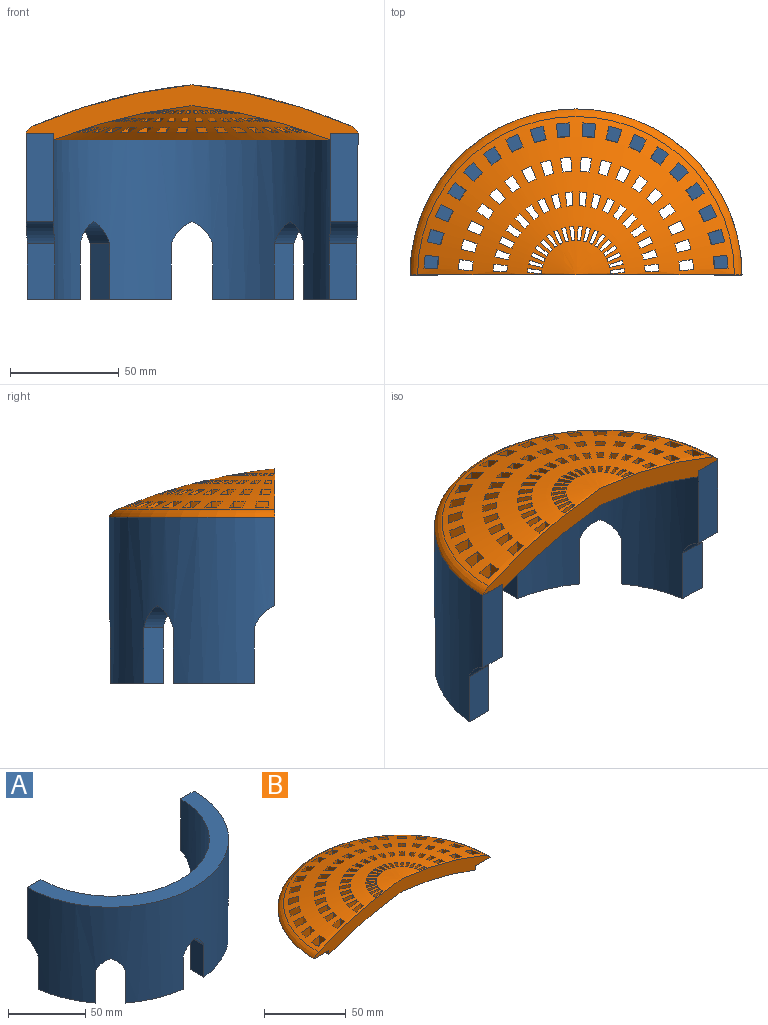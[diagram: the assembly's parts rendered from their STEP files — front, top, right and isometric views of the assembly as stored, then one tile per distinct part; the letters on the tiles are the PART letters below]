
ASSEMBLY  parts=2 mates=1
PART A: 25 faces, bbox 152.4x76.2x76.2 mm
  f0: cylinder r=63.75mm len=127.51mm, axis (0,0,-1), area 12814.7mm2, adj f2,f3,f4,f5,f6,f7,f8,f9
  f1: cylinder r=76.2mm len=152.4mm, axis (0,0,-1), area 15796.6mm2, adj f2,f3,f4,f5,f6,f7,f8,f9
  f2: plane 152.4x76.2mm, normal (0,0,1), area 2736.1mm2, adj f0,f1,f23,f24
  f3: plane 25.4x12.56mm, normal (0,1,0), area 319.1mm2, adj f0,f1,f4,f5
  f4: cylinder r=16.44mm len=13.16mm, axis (-1,0,0), area 179.7mm2, adj f0,f1,f3,f24
  f5: plane 37.2x24.29mm, normal (0,0,-1), area 446.2mm2, adj f0,f1,f3,f6
  f6: plane 25.4x8.88mm, normal (-0.71,-0.71,0), area 319.1mm2, adj f0,f1,f5,f9
  f7: plane 25.4x8.88mm, normal (0.71,0.71,0), area 319.1mm2, adj f0,f1,f8,f10
  f8: cylinder r=16.44mm len=16.04mm, axis (-0.71,0.71,0), area 179.7mm2, adj f0,f1,f7,f9
  f9: cylinder r=16.44mm len=16.04mm, axis (-0.71,0.71,0), area 179.7mm2, adj f0,f1,f6,f8
  f10: plane 37.2x24.29mm, normal (0,0,-1), area 446.2mm2, adj f0,f1,f7,f11
  f11: plane 25.4x12.56mm, normal (-1,0,0), area 319.1mm2, adj f0,f1,f10,f14
  f12: plane 25.4x12.56mm, normal (1,0,0), area 319.1mm2, adj f0,f1,f13,f15
  f13: cylinder r=16.44mm len=13.16mm, axis (0,1,0), area 179.7mm2, adj f0,f1,f12,f14
  f14: cylinder r=16.44mm len=13.16mm, axis (0,1,0), area 179.7mm2, adj f0,f1,f11,f13
  f15: plane 37.2x24.29mm, normal (0,0,-1), area 446.2mm2, adj f0,f1,f12,f16
  f16: plane 25.4x8.88mm, normal (-0.71,0.71,0), area 319.1mm2, adj f0,f1,f15,f19
  f17: plane 25.4x8.88mm, normal (0.71,-0.71,0), area 319.1mm2, adj f0,f1,f18,f20
  f18: cylinder r=16.44mm len=16.04mm, axis (0.71,0.71,0), area 179.7mm2, adj f0,f1,f17,f19
  f19: cylinder r=16.44mm len=16.04mm, axis (0.71,0.71,0), area 179.7mm2, adj f0,f1,f16,f18
  f20: plane 37.2x24.29mm, normal (0,0,-1), area 446.2mm2, adj f0,f1,f17,f21
  f21: plane 25.4x12.56mm, normal (0,1,0), area 319.1mm2, adj f0,f1,f20,f22
  f22: cylinder r=16.44mm len=13.16mm, axis (1,0,0), area 179.7mm2, adj f0,f1,f21,f23
  f23: plane 40.64x12.45mm, normal (0,1,0), area 505.7mm2, adj f0,f1,f2,f22
  f24: plane 40.64x12.45mm, normal (0,1,0), area 505.7mm2, adj f0,f1,f2,f4
PART B: 276 faces, bbox 166.3x83.1x25.3 mm
  f0: revolved ~145.41x72.71mm, area 6921.5mm2, adj f3,f4,f5,f6,f7,f8,f9,f10
  f1: plane 152.4x76.2mm, normal (0,0,-1), area 2121.8mm2, adj f3,f4,f5,f222,f223,f224,f225,f226
  f2: revolved ~127x63.5mm, area 5531.8mm2, adj f4,f5,f6,f7,f8,f9,f10,f11
  f3: torus R=70.05mm, axis (0,0,1), area 1172.7mm2, adj f0,f1,f5
  f4: cylinder r=63.5mm len=127mm, axis (0,0,1), area 1327.7mm2, adj f0,f1,f2,f5,f223,f224,f226,f227
  f5: plane 152.4x25.31mm, normal (0,-1,0), area 1361.2mm2, adj f0,f1,f2,f3,f4
  f6: cylinder r=31.75mm len=9.8mm, axis (0,0,1), area 27.1mm2, adj f0,f2,f7,f9
  f7: plane 11.45x6.3mm, normal (-0.99,0.13,0), area 62.4mm2, adj f0,f2,f6,f8
  f8: cylinder r=38.1mm len=9.86mm, axis (0,0,1), area 32.8mm2, adj f0,f2,f7,f9
  f9: plane 11.45x6.34mm, normal (1,-0.04,0), area 62.4mm2, adj f0,f2,f6,f8
  f10: plane 12.11x6.2mm, normal (0.22,0.98,0), area 63.7mm2, adj f0,f2,f11,f13
  f11: cylinder r=47.62mm len=9.98mm, axis (0,0,1), area 41.5mm2, adj f0,f2,f10,f12
  f12: plane 12.11x6.06mm, normal (-0.3,-0.95,0), area 63.7mm2, adj f0,f2,f11,f13
  f13: cylinder r=53.98mm len=10.07mm, axis (0,0,1), area 47.4mm2, adj f0,f2,f10,f12
  f14: plane 11.45x5.87mm, normal (0.38,0.92,0), area 62.4mm2, adj f0,f2,f15,f17
  f15: cylinder r=31.75mm len=9.8mm, axis (0,0,1), area 27.1mm2, adj f0,f2,f14,f16
  f16: plane 11.45x5.63mm, normal (-0.46,-0.89,0), area 62.4mm2, adj f0,f2,f15,f17
  f17: cylinder r=38.1mm len=9.86mm, axis (0,0,1), area 32.8mm2, adj f0,f2,f14,f16
  f18: cylinder r=38.1mm len=9.86mm, axis (0,0,1), area 32.8mm2, adj f0,f2,f19,f21
  f19: plane 11.45x6.2mm, normal (0.22,0.98,0), area 62.4mm2, adj f0,f2,f18,f20
  f20: cylinder r=31.75mm len=9.8mm, axis (0,0,1), area 27.1mm2, adj f0,f2,f19,f21
  f21: plane 11.45x6.06mm, normal (-0.3,-0.95,0), area 62.4mm2, adj f0,f2,f18,f20
  f22: plane 12.11x6.34mm, normal (-0.04,1,0), area 63.7mm2, adj f0,f2,f23,f25
  f23: cylinder r=53.98mm len=10.07mm, axis (0,0,1), area 47.4mm2, adj f0,f2,f22,f24
  f24: plane 12.11x6.3mm, normal (0.13,-0.99,0), area 63.7mm2, adj f0,f2,f23,f25
  f25: cylinder r=47.62mm len=9.98mm, axis (0,0,1), area 41.5mm2, adj f0,f2,f22,f24
  f26: plane 10.86x6.2mm, normal (0.22,0.98,0), area 61.5mm2, adj f0,f2,f27,f29
  f27: cylinder r=15.88mm len=9.66mm, axis (0,0,1), area 13.4mm2, adj f0,f2,f26,f28
  f28: plane 10.86x6.06mm, normal (-0.3,-0.95,0), area 61.5mm2, adj f0,f2,f27,f29
  f29: cylinder r=22.23mm len=9.71mm, axis (0,0,1), area 18.8mm2, adj f0,f2,f26,f28
  f30: cylinder r=22.23mm len=9.71mm, axis (0,0,1), area 18.8mm2, adj f0,f2,f31,f33
  f31: plane 10.86x5.36mm, normal (0.54,0.84,0), area 61.5mm2, adj f0,f2,f30,f32
  f32: cylinder r=15.88mm len=9.66mm, axis (0,0,1), area 13.4mm2, adj f0,f2,f31,f33
  f33: plane 10.86x5.04mm, normal (-0.61,-0.79,0), area 61.5mm2, adj f0,f2,f30,f32
  f34: plane 10.86x5.87mm, normal (0.38,0.92,0), area 61.5mm2, adj f0,f2,f35,f37
  f35: cylinder r=15.88mm len=9.66mm, axis (0,0,1), area 13.4mm2, adj f0,f2,f34,f36
  f36: plane 10.86x5.63mm, normal (-0.46,-0.89,0), area 61.5mm2, adj f0,f2,f35,f37
  f37: cylinder r=22.23mm len=9.71mm, axis (0,0,1), area 18.8mm2, adj f0,f2,f34,f36
  f38: plane 11.45x4.68mm, normal (-0.68,0.74,0), area 62.4mm2, adj f0,f2,f39,f41
  f39: cylinder r=38.1mm len=9.86mm, axis (0,0,1), area 32.8mm2, adj f0,f2,f38,f40
  f40: plane 11.45x4.68mm, normal (0.74,-0.68,0), area 62.4mm2, adj f0,f2,f39,f41
  f41: cylinder r=31.75mm len=9.8mm, axis (0,0,1), area 27.1mm2, adj f0,f2,f38,f40
  f42: plane 10.86x6.06mm, normal (-0.95,0.3,0), area 61.5mm2, adj f0,f2,f43,f45
  f43: cylinder r=22.23mm len=9.71mm, axis (0,0,1), area 18.8mm2, adj f0,f2,f42,f44
  f44: plane 10.86x6.2mm, normal (0.98,-0.22,0), area 61.5mm2, adj f0,f2,f43,f45
  f45: cylinder r=15.88mm len=9.66mm, axis (0,0,1), area 13.4mm2, adj f0,f2,f42,f44
  f46: plane 10.86x5.04mm, normal (-0.79,0.61,0), area 61.5mm2, adj f0,f2,f47,f49
  f47: cylinder r=22.23mm len=9.71mm, axis (0,0,1), area 18.8mm2, adj f0,f2,f46,f48
  f48: plane 10.86x5.36mm, normal (0.84,-0.54,0), area 61.5mm2, adj f0,f2,f47,f49
  f49: cylinder r=15.88mm len=9.66mm, axis (0,0,1), area 13.4mm2, adj f0,f2,f46,f48
  f50: plane 10.86x5.63mm, normal (-0.89,0.46,0), area 61.5mm2, adj f0,f2,f51,f53
  f51: cylinder r=22.23mm len=9.71mm, axis (0,0,1), area 18.8mm2, adj f0,f2,f50,f52
  f52: plane 10.86x5.87mm, normal (0.92,-0.38,0), area 61.5mm2, adj f0,f2,f51,f53
  f53: cylinder r=15.88mm len=9.66mm, axis (0,0,1), area 13.4mm2, adj f0,f2,f50,f52
  f54: plane 12.11x5.87mm, normal (-0.38,0.92,0), area 63.7mm2, adj f0,f2,f55,f57
  f55: cylinder r=53.98mm len=10.07mm, axis (0,0,1), area 47.4mm2, adj f0,f2,f54,f56
  f56: plane 12.11x5.63mm, normal (0.46,-0.89,0), area 63.7mm2, adj f0,f2,f55,f57
  f57: cylinder r=47.62mm len=9.98mm, axis (0,0,1), area 41.5mm2, adj f0,f2,f54,f56
  f58: plane 11.45x6.06mm, normal (-0.95,0.3,0), area 62.4mm2, adj f0,f2,f59,f61
  f59: cylinder r=38.1mm len=9.86mm, axis (0,0,1), area 32.8mm2, adj f0,f2,f58,f60
  f60: plane 11.45x6.2mm, normal (0.98,-0.22,0), area 62.4mm2, adj f0,f2,f59,f61
  f61: cylinder r=31.75mm len=9.8mm, axis (0,0,1), area 27.1mm2, adj f0,f2,f58,f60
  f62: plane 11.45x5.04mm, normal (-0.79,0.61,0), area 62.4mm2, adj f0,f2,f63,f65
  f63: cylinder r=38.1mm len=9.86mm, axis (0,0,1), area 32.8mm2, adj f0,f2,f62,f64
  f64: plane 11.45x5.36mm, normal (0.84,-0.54,0), area 62.4mm2, adj f0,f2,f63,f65
  f65: cylinder r=31.75mm len=9.8mm, axis (0,0,1), area 27.1mm2, adj f0,f2,f62,f64
  f66: plane 11.45x5.63mm, normal (-0.89,0.46,0), area 62.4mm2, adj f0,f2,f67,f69
  f67: cylinder r=38.1mm len=9.86mm, axis (0,0,1), area 32.8mm2, adj f0,f2,f66,f68
  f68: plane 11.45x5.87mm, normal (0.92,-0.38,0), area 62.4mm2, adj f0,f2,f67,f69
  f69: cylinder r=31.75mm len=9.8mm, axis (0,0,1), area 27.1mm2, adj f0,f2,f66,f68
  f70: plane 10.86x5.36mm, normal (-0.54,0.84,0), area 61.5mm2, adj f0,f2,f71,f73
  f71: cylinder r=22.23mm len=9.71mm, axis (0,0,1), area 18.8mm2, adj f0,f2,f70,f72
  f72: plane 10.86x5.04mm, normal (0.61,-0.79,0), area 61.5mm2, adj f0,f2,f71,f73
  f73: cylinder r=15.88mm len=9.66mm, axis (0,0,1), area 13.4mm2, adj f0,f2,f70,f72
  f74: cylinder r=31.75mm len=9.8mm, axis (0,0,1), area 27.1mm2, adj f0,f2,f75,f77
  f75: plane 11.45x4.68mm, normal (-0.74,-0.68,0), area 62.4mm2, adj f0,f2,f74,f76
  f76: cylinder r=38.1mm len=9.86mm, axis (0,0,1), area 32.8mm2, adj f0,f2,f75,f77
  f77: plane 11.45x4.68mm, normal (0.68,0.74,0), area 62.4mm2, adj f0,f2,f74,f76
  f78: cylinder r=31.75mm len=9.8mm, axis (0,0,1), area 27.1mm2, adj f0,f2,f79,f81
  f79: plane 11.45x5.36mm, normal (-0.84,-0.54,0), area 62.4mm2, adj f0,f2,f78,f80
  f80: cylinder r=38.1mm len=9.86mm, axis (0,0,1), area 32.8mm2, adj f0,f2,f79,f81
  f81: plane 11.45x5.04mm, normal (0.79,0.61,0), area 62.4mm2, adj f0,f2,f78,f80
  f82: cylinder r=15.88mm len=9.66mm, axis (0,0,1), area 13.4mm2, adj f0,f2,f83,f85
  f83: plane 10.86x6.2mm, normal (-0.98,-0.22,0), area 61.5mm2, adj f0,f2,f82,f84
  f84: cylinder r=22.23mm len=9.71mm, axis (0,0,1), area 18.8mm2, adj f0,f2,f83,f85
  f85: plane 10.86x6.06mm, normal (0.95,0.3,0), area 61.5mm2, adj f0,f2,f82,f84
  f86: plane 10.86x4.68mm, normal (-0.68,0.74,0), area 61.5mm2, adj f0,f2,f87,f89
  f87: cylinder r=22.23mm len=9.71mm, axis (0,0,1), area 18.8mm2, adj f0,f2,f86,f88
  f88: plane 10.86x4.68mm, normal (0.74,-0.68,0), area 61.5mm2, adj f0,f2,f87,f89
  f89: cylinder r=15.88mm len=9.66mm, axis (0,0,1), area 13.4mm2, adj f0,f2,f86,f88
  f90: plane 11.45x5.36mm, normal (-0.54,0.84,0), area 62.4mm2, adj f0,f2,f91,f93
  f91: cylinder r=38.1mm len=9.86mm, axis (0,0,1), area 32.8mm2, adj f0,f2,f90,f92
  f92: plane 11.45x5.04mm, normal (0.61,-0.79,0), area 62.4mm2, adj f0,f2,f91,f93
  f93: cylinder r=31.75mm len=9.8mm, axis (0,0,1), area 27.1mm2, adj f0,f2,f90,f92
  f94: plane 11.45x5.87mm, normal (-0.38,0.92,0), area 62.4mm2, adj f0,f2,f95,f97
  f95: cylinder r=38.1mm len=9.86mm, axis (0,0,1), area 32.8mm2, adj f0,f2,f94,f96
  f96: plane 11.45x5.63mm, normal (0.46,-0.89,0), area 62.4mm2, adj f0,f2,f95,f97
  f97: cylinder r=31.75mm len=9.8mm, axis (0,0,1), area 27.1mm2, adj f0,f2,f94,f96
  f98: plane 12.11x6.2mm, normal (-0.22,0.98,0), area 63.7mm2, adj f0,f2,f99,f101
  f99: cylinder r=53.98mm len=10.07mm, axis (0,0,1), area 47.4mm2, adj f0,f2,f98,f100
  f100: plane 12.11x6.06mm, normal (0.3,-0.95,0), area 63.7mm2, adj f0,f2,f99,f101
  f101: cylinder r=47.62mm len=9.98mm, axis (0,0,1), area 41.5mm2, adj f0,f2,f98,f100
  f102: plane 10.86x6.34mm, normal (1,-0.04,0), area 61.5mm2, adj f0,f2,f103,f105
  f103: cylinder r=15.88mm len=9.66mm, axis (0,0,1), area 13.4mm2, adj f0,f2,f102,f104
  f104: plane 10.86x6.3mm, normal (-0.99,0.13,0), area 61.5mm2, adj f0,f2,f103,f105
  f105: cylinder r=22.23mm len=9.71mm, axis (0,0,1), area 18.8mm2, adj f0,f2,f102,f104
  f106: plane 12.11x6.34mm, normal (1,-0.04,0), area 63.7mm2, adj f0,f2,f107,f109
  f107: cylinder r=47.62mm len=9.98mm, axis (0,0,1), area 41.5mm2, adj f0,f2,f106,f108
  f108: plane 12.11x6.3mm, normal (-0.99,0.13,0), area 63.7mm2, adj f0,f2,f107,f109
  f109: cylinder r=53.98mm len=10.07mm, axis (0,0,1), area 47.4mm2, adj f0,f2,f106,f108
  f110: plane 12.11x5.63mm, normal (-0.89,0.46,0), area 63.7mm2, adj f0,f2,f111,f113
  f111: cylinder r=53.98mm len=10.07mm, axis (0,0,1), area 47.4mm2, adj f0,f2,f110,f112
  f112: plane 12.11x5.87mm, normal (0.92,-0.38,0), area 63.7mm2, adj f0,f2,f111,f113
  f113: cylinder r=47.62mm len=9.98mm, axis (0,0,1), area 41.5mm2, adj f0,f2,f110,f112
  f114: plane 12.11x5.04mm, normal (-0.79,0.61,0), area 63.7mm2, adj f0,f2,f115,f117
  f115: cylinder r=53.98mm len=10.07mm, axis (0,0,1), area 47.4mm2, adj f0,f2,f114,f116
  f116: plane 12.11x5.36mm, normal (0.84,-0.54,0), area 63.7mm2, adj f0,f2,f115,f117
  f117: cylinder r=47.62mm len=9.98mm, axis (0,0,1), area 41.5mm2, adj f0,f2,f114,f116
  f118: plane 12.11x5.36mm, normal (-0.54,0.84,0), area 63.7mm2, adj f0,f2,f119,f121
  f119: cylinder r=53.98mm len=10.07mm, axis (0,0,1), area 47.4mm2, adj f0,f2,f118,f120
  f120: plane 12.11x5.04mm, normal (0.61,-0.79,0), area 63.7mm2, adj f0,f2,f119,f121
  f121: cylinder r=47.62mm len=9.98mm, axis (0,0,1), area 41.5mm2, adj f0,f2,f118,f120
  f122: plane 12.11x4.68mm, normal (-0.68,0.74,0), area 63.7mm2, adj f0,f2,f123,f125
  f123: cylinder r=53.98mm len=10.07mm, axis (0,0,1), area 47.4mm2, adj f0,f2,f122,f124
  f124: plane 12.11x4.68mm, normal (0.74,-0.68,0), area 63.7mm2, adj f0,f2,f123,f125
  f125: cylinder r=47.62mm len=9.98mm, axis (0,0,1), area 41.5mm2, adj f0,f2,f122,f124
  f126: plane 12.11x6.06mm, normal (-0.95,0.3,0), area 63.7mm2, adj f0,f2,f127,f129
  f127: cylinder r=53.98mm len=10.07mm, axis (0,0,1), area 47.4mm2, adj f0,f2,f126,f128
  f128: plane 12.11x6.2mm, normal (0.98,-0.22,0), area 63.7mm2, adj f0,f2,f127,f129
  f129: cylinder r=47.62mm len=9.98mm, axis (0,0,1), area 41.5mm2, adj f0,f2,f126,f128
  f130: plane 12.11x6.34mm, normal (0.04,1,0), area 63.7mm2, adj f0,f2,f131,f133
  f131: cylinder r=47.62mm len=9.98mm, axis (0,0,1), area 41.5mm2, adj f0,f2,f130,f132
  f132: plane 12.11x6.3mm, normal (-0.13,-0.99,0), area 63.7mm2, adj f0,f2,f131,f133
  f133: cylinder r=53.98mm len=10.07mm, axis (0,0,1), area 47.4mm2, adj f0,f2,f130,f132
  f134: plane 11.45x6.34mm, normal (-0.04,1,0), area 62.4mm2, adj f0,f2,f135,f137
  f135: cylinder r=38.1mm len=9.86mm, axis (0,0,1), area 32.8mm2, adj f0,f2,f134,f136
  f136: plane 11.45x6.3mm, normal (0.13,-0.99,0), area 62.4mm2, adj f0,f2,f135,f137
  f137: cylinder r=31.75mm len=9.8mm, axis (0,0,1), area 27.1mm2, adj f0,f2,f134,f136
  f138: plane 11.45x6.2mm, normal (-0.22,0.98,0), area 62.4mm2, adj f0,f2,f139,f141
  f139: cylinder r=38.1mm len=9.86mm, axis (0,0,1), area 32.8mm2, adj f0,f2,f138,f140
  f140: plane 11.45x6.06mm, normal (0.3,-0.95,0), area 62.4mm2, adj f0,f2,f139,f141
  f141: cylinder r=31.75mm len=9.8mm, axis (0,0,1), area 27.1mm2, adj f0,f2,f138,f140
  f142: plane 10.86x6.34mm, normal (-0.04,1,0), area 61.5mm2, adj f0,f2,f143,f145
  f143: cylinder r=22.23mm len=9.71mm, axis (0,0,1), area 18.8mm2, adj f0,f2,f142,f144
  f144: plane 10.86x6.3mm, normal (0.13,-0.99,0), area 61.5mm2, adj f0,f2,f143,f145
  f145: cylinder r=15.88mm len=9.66mm, axis (0,0,1), area 13.4mm2, adj f0,f2,f142,f144
  f146: plane 10.86x6.2mm, normal (-0.22,0.98,0), area 61.5mm2, adj f0,f2,f147,f149
  f147: cylinder r=22.23mm len=9.71mm, axis (0,0,1), area 18.8mm2, adj f0,f2,f146,f148
  f148: plane 10.86x6.06mm, normal (0.3,-0.95,0), area 61.5mm2, adj f0,f2,f147,f149
  f149: cylinder r=15.88mm len=9.66mm, axis (0,0,1), area 13.4mm2, adj f0,f2,f146,f148
  f150: plane 10.86x5.87mm, normal (-0.38,0.92,0), area 61.5mm2, adj f0,f2,f151,f153
  f151: cylinder r=22.23mm len=9.71mm, axis (0,0,1), area 18.8mm2, adj f0,f2,f150,f152
  f152: plane 10.86x5.63mm, normal (0.46,-0.89,0), area 61.5mm2, adj f0,f2,f151,f153
  f153: cylinder r=15.88mm len=9.66mm, axis (0,0,1), area 13.4mm2, adj f0,f2,f150,f152
  f154: cylinder r=22.23mm len=9.71mm, axis (0,0,1), area 18.8mm2, adj f0,f2,f155,f157
  f155: plane 10.86x6.3mm, normal (0.99,0.13,0), area 61.5mm2, adj f0,f2,f154,f156
  f156: cylinder r=15.88mm len=9.66mm, axis (0,0,1), area 13.4mm2, adj f0,f2,f155,f157
  f157: plane 10.86x6.34mm, normal (-1,-0.04,0), area 61.5mm2, adj f0,f2,f154,f156
  f158: cylinder r=38.1mm len=9.86mm, axis (0,0,1), area 32.8mm2, adj f0,f2,f159,f161
  f159: plane 11.45x6.3mm, normal (0.99,0.13,0), area 62.4mm2, adj f0,f2,f158,f160
  f160: cylinder r=31.75mm len=9.8mm, axis (0,0,1), area 27.1mm2, adj f0,f2,f159,f161
  f161: plane 11.45x6.34mm, normal (-1,-0.04,0), area 62.4mm2, adj f0,f2,f158,f160
  f162: plane 11.45x6.06mm, normal (0.95,0.3,0), area 62.4mm2, adj f0,f2,f163,f165
  f163: cylinder r=31.75mm len=9.8mm, axis (0,0,1), area 27.1mm2, adj f0,f2,f162,f164
  f164: plane 11.45x6.2mm, normal (-0.98,-0.22,0), area 62.4mm2, adj f0,f2,f163,f165
  f165: cylinder r=38.1mm len=9.86mm, axis (0,0,1), area 32.8mm2, adj f0,f2,f162,f164
  f166: plane 10.86x5.63mm, normal (0.89,0.46,0), area 61.5mm2, adj f0,f2,f167,f169
  f167: cylinder r=15.88mm len=9.66mm, axis (0,0,1), area 13.4mm2, adj f0,f2,f166,f168
  f168: plane 10.86x5.87mm, normal (-0.92,-0.38,0), area 61.5mm2, adj f0,f2,f167,f169
  f169: cylinder r=22.23mm len=9.71mm, axis (0,0,1), area 18.8mm2, adj f0,f2,f166,f168
  f170: cylinder r=31.75mm len=9.8mm, axis (0,0,1), area 27.1mm2, adj f0,f2,f171,f173
  f171: plane 11.45x5.87mm, normal (-0.92,-0.38,0), area 62.4mm2, adj f0,f2,f170,f172
  f172: cylinder r=38.1mm len=9.86mm, axis (0,0,1), area 32.8mm2, adj f0,f2,f171,f173
  f173: plane 11.45x5.63mm, normal (0.89,0.46,0), area 62.4mm2, adj f0,f2,f170,f172
  f174: plane 12.11x5.87mm, normal (0.38,0.92,0), area 63.7mm2, adj f0,f2,f175,f177
  f175: cylinder r=47.62mm len=9.98mm, axis (0,0,1), area 41.5mm2, adj f0,f2,f174,f176
  f176: plane 12.11x5.63mm, normal (-0.46,-0.89,0), area 63.7mm2, adj f0,f2,f175,f177
  f177: cylinder r=53.98mm len=10.07mm, axis (0,0,1), area 47.4mm2, adj f0,f2,f174,f176
  f178: plane 12.11x5.36mm, normal (0.54,0.84,0), area 63.7mm2, adj f0,f2,f179,f181
  f179: cylinder r=47.62mm len=9.98mm, axis (0,0,1), area 41.5mm2, adj f0,f2,f178,f180
  f180: plane 12.11x5.04mm, normal (-0.61,-0.79,0), area 63.7mm2, adj f0,f2,f179,f181
  f181: cylinder r=53.98mm len=10.07mm, axis (0,0,1), area 47.4mm2, adj f0,f2,f178,f180
  f182: plane 10.86x5.04mm, normal (0.79,0.61,0), area 61.5mm2, adj f0,f2,f183,f185
  f183: cylinder r=15.88mm len=9.66mm, axis (0,0,1), area 13.4mm2, adj f0,f2,f182,f184
  f184: plane 10.86x5.36mm, normal (-0.84,-0.54,0), area 61.5mm2, adj f0,f2,f183,f185
  f185: cylinder r=22.23mm len=9.71mm, axis (0,0,1), area 18.8mm2, adj f0,f2,f182,f184
  f186: plane 12.11x6.3mm, normal (0.99,0.13,0), area 63.7mm2, adj f0,f2,f187,f189
  f187: cylinder r=47.62mm len=9.98mm, axis (0,0,1), area 41.5mm2, adj f0,f2,f186,f188
  f188: plane 12.11x6.34mm, normal (-1,-0.04,0), area 63.7mm2, adj f0,f2,f187,f189
  f189: cylinder r=53.98mm len=10.07mm, axis (0,0,1), area 47.4mm2, adj f0,f2,f186,f188
  f190: cylinder r=31.75mm len=9.8mm, axis (0,0,1), area 27.1mm2, adj f0,f2,f191,f193
  f191: plane 11.45x5.04mm, normal (-0.61,-0.79,0), area 62.4mm2, adj f0,f2,f190,f192
  f192: cylinder r=38.1mm len=9.86mm, axis (0,0,1), area 32.8mm2, adj f0,f2,f191,f193
  f193: plane 11.45x5.36mm, normal (0.54,0.84,0), area 62.4mm2, adj f0,f2,f190,f192
  f194: cylinder r=47.62mm len=9.98mm, axis (0,0,1), area 41.5mm2, adj f0,f2,f195,f197
  f195: plane 12.11x5.36mm, normal (-0.84,-0.54,0), area 63.7mm2, adj f0,f2,f194,f196
  f196: cylinder r=53.98mm len=10.07mm, axis (0,0,1), area 47.4mm2, adj f0,f2,f195,f197
  f197: plane 12.11x5.04mm, normal (0.79,0.61,0), area 63.7mm2, adj f0,f2,f194,f196
  f198: plane 10.86x6.34mm, normal (0.04,1,0), area 61.5mm2, adj f0,f2,f199,f201
  f199: cylinder r=15.88mm len=9.66mm, axis (0,0,1), area 13.4mm2, adj f0,f2,f198,f200
  f200: plane 10.86x6.3mm, normal (-0.13,-0.99,0), area 61.5mm2, adj f0,f2,f199,f201
  f201: cylinder r=22.23mm len=9.71mm, axis (0,0,1), area 18.8mm2, adj f0,f2,f198,f200
  f202: plane 10.86x4.68mm, normal (0.68,0.74,0), area 61.5mm2, adj f0,f2,f203,f205
  f203: cylinder r=15.88mm len=9.66mm, axis (0,0,1), area 13.4mm2, adj f0,f2,f202,f204
  f204: plane 10.86x4.68mm, normal (-0.74,-0.68,0), area 61.5mm2, adj f0,f2,f203,f205
  f205: cylinder r=22.23mm len=9.71mm, axis (0,0,1), area 18.8mm2, adj f0,f2,f202,f204
  f206: plane 12.11x6.06mm, normal (0.95,0.3,0), area 63.7mm2, adj f0,f2,f207,f209
  f207: cylinder r=47.62mm len=9.98mm, axis (0,0,1), area 41.5mm2, adj f0,f2,f206,f208
  f208: plane 12.11x6.2mm, normal (-0.98,-0.22,0), area 63.7mm2, adj f0,f2,f207,f209
  f209: cylinder r=53.98mm len=10.07mm, axis (0,0,1), area 47.4mm2, adj f0,f2,f206,f208
  f210: cylinder r=31.75mm len=9.8mm, axis (0,0,1), area 27.1mm2, adj f0,f2,f211,f213
  f211: plane 11.45x6.3mm, normal (-0.13,-0.99,0), area 62.4mm2, adj f0,f2,f210,f212
  f212: cylinder r=38.1mm len=9.86mm, axis (0,0,1), area 32.8mm2, adj f0,f2,f211,f213
  f213: plane 11.45x6.34mm, normal (0.04,1,0), area 62.4mm2, adj f0,f2,f210,f212
  f214: plane 12.11x4.68mm, normal (0.68,0.74,0), area 63.7mm2, adj f0,f2,f215,f217
  f215: cylinder r=47.62mm len=9.98mm, axis (0,0,1), area 41.5mm2, adj f0,f2,f214,f216
  f216: plane 12.11x4.68mm, normal (-0.74,-0.68,0), area 63.7mm2, adj f0,f2,f215,f217
  f217: cylinder r=53.98mm len=10.07mm, axis (0,0,1), area 47.4mm2, adj f0,f2,f214,f216
  f218: plane 12.11x5.63mm, normal (0.89,0.46,0), area 63.7mm2, adj f0,f2,f219,f221
  f219: cylinder r=47.62mm len=9.98mm, axis (0,0,1), area 41.5mm2, adj f0,f2,f218,f220
  f220: plane 12.11x5.87mm, normal (-0.92,-0.38,0), area 63.7mm2, adj f0,f2,f219,f221
  f221: cylinder r=53.98mm len=10.07mm, axis (0,0,1), area 47.4mm2, adj f0,f2,f218,f220
  f222: cylinder r=69.85mm len=6.07mm, axis (0,0,1), area 28.1mm2, adj f0,f1,f223,f224
  f223: plane 7.14x6.3mm, normal (-0.99,0.13,0), area 37.4mm2, adj f0,f1,f4,f222
  f224: plane 7.14x6.34mm, normal (1,-0.04,0), area 37.4mm2, adj f0,f1,f4,f222
  f225: cylinder r=69.85mm len=5.89mm, axis (0,0,1), area 28.1mm2, adj f0,f1,f226,f227
  f226: plane 7.14x6.06mm, normal (-0.95,0.3,0), area 37.4mm2, adj f0,f1,f4,f225
  f227: plane 7.14x6.2mm, normal (0.98,-0.22,0), area 37.4mm2, adj f0,f1,f4,f225
  f228: cylinder r=69.85mm len=5.52mm, axis (0,0,1), area 28.1mm2, adj f0,f1,f229,f230
  f229: plane 7.14x5.63mm, normal (-0.89,0.46,0), area 37.4mm2, adj f0,f1,f4,f228
  f230: plane 7.14x5.87mm, normal (0.92,-0.38,0), area 37.4mm2, adj f0,f1,f4,f228
  f231: cylinder r=69.85mm len=4.99mm, axis (0,0,1), area 28.1mm2, adj f0,f1,f232,f233
  f232: plane 7.14x5.04mm, normal (-0.79,0.61,0), area 37.4mm2, adj f0,f1,f4,f231
  f233: plane 7.14x5.36mm, normal (0.84,-0.54,0), area 37.4mm2, adj f0,f1,f4,f231
  f234: cylinder r=69.85mm len=4.62mm, axis (0,0,1), area 28.1mm2, adj f0,f1,f235,f236
  f235: plane 7.14x4.68mm, normal (-0.68,0.74,0), area 37.4mm2, adj f0,f1,f4,f234
  f236: plane 7.14x4.68mm, normal (0.74,-0.68,0), area 37.4mm2, adj f0,f1,f4,f234
  f237: cylinder r=69.85mm len=4.99mm, axis (0,0,1), area 28.1mm2, adj f0,f1,f238,f239
  f238: plane 7.14x5.36mm, normal (-0.54,0.84,0), area 37.4mm2, adj f0,f1,f4,f237
  f239: plane 7.14x5.04mm, normal (0.61,-0.79,0), area 37.4mm2, adj f0,f1,f4,f237
  f240: cylinder r=69.85mm len=5.52mm, axis (0,0,1), area 28.1mm2, adj f0,f1,f241,f242
  f241: plane 7.14x5.87mm, normal (-0.38,0.92,0), area 37.4mm2, adj f0,f1,f4,f240
  f242: plane 7.14x5.63mm, normal (0.46,-0.89,0), area 37.4mm2, adj f0,f1,f4,f240
  f243: cylinder r=69.85mm len=5.89mm, axis (0,0,1), area 28.1mm2, adj f0,f1,f244,f245
  f244: plane 7.14x6.2mm, normal (-0.22,0.98,0), area 37.4mm2, adj f0,f1,f4,f243
  f245: plane 7.14x6.06mm, normal (0.3,-0.95,0), area 37.4mm2, adj f0,f1,f4,f243
  f246: cylinder r=69.85mm len=6.07mm, axis (0,0,1), area 28.1mm2, adj f0,f1,f247,f248
  f247: plane 7.14x6.34mm, normal (-0.04,1,0), area 37.4mm2, adj f0,f1,f4,f246
  f248: plane 7.14x6.3mm, normal (0.13,-0.99,0), area 37.4mm2, adj f0,f1,f4,f246
  f249: cylinder r=69.85mm len=4.99mm, axis (0,0,1), area 28.1mm2, adj f0,f1,f250,f251
  f250: plane 7.14x5.04mm, normal (0.79,0.61,0), area 37.4mm2, adj f0,f1,f4,f249
  f251: plane 7.14x5.36mm, normal (-0.84,-0.54,0), area 37.4mm2, adj f0,f1,f4,f249
  f252: cylinder r=69.85mm len=5.52mm, axis (0,0,1), area 28.1mm2, adj f0,f1,f253,f254
  f253: plane 7.14x5.87mm, normal (-0.92,-0.38,0), area 37.4mm2, adj f0,f1,f4,f252
  f254: plane 7.14x5.63mm, normal (0.89,0.46,0), area 37.4mm2, adj f0,f1,f4,f252
  f255: cylinder r=69.85mm len=5.52mm, axis (0,0,1), area 28.1mm2, adj f0,f1,f256,f257
  f256: plane 7.14x5.87mm, normal (0.38,0.92,0), area 37.4mm2, adj f0,f1,f4,f255
  f257: plane 7.14x5.63mm, normal (-0.46,-0.89,0), area 37.4mm2, adj f0,f1,f4,f255
  f258: cylinder r=69.85mm len=5.89mm, axis (0,0,1), area 28.1mm2, adj f0,f1,f259,f260
  f259: plane 7.14x6.2mm, normal (0.22,0.98,0), area 37.4mm2, adj f0,f1,f4,f258
  f260: plane 7.14x6.06mm, normal (-0.3,-0.95,0), area 37.4mm2, adj f0,f1,f4,f258
  f261: cylinder r=69.85mm len=6.07mm, axis (0,0,1), area 28.1mm2, adj f0,f1,f262,f263
  f262: plane 7.14x6.34mm, normal (0.04,1,0), area 37.4mm2, adj f0,f1,f4,f261
  f263: plane 7.14x6.3mm, normal (-0.13,-0.99,0), area 37.4mm2, adj f0,f1,f4,f261
  f264: cylinder r=69.85mm len=4.62mm, axis (0,0,1), area 28.1mm2, adj f0,f1,f265,f266
  f265: plane 7.14x4.68mm, normal (-0.74,-0.68,0), area 37.4mm2, adj f0,f1,f4,f264
  f266: plane 7.14x4.68mm, normal (0.68,0.74,0), area 37.4mm2, adj f0,f1,f4,f264
  f267: cylinder r=69.85mm len=5.89mm, axis (0,0,1), area 28.1mm2, adj f0,f1,f268,f269
  f268: plane 7.14x6.2mm, normal (-0.98,-0.22,0), area 37.4mm2, adj f0,f1,f4,f267
  f269: plane 7.14x6.06mm, normal (0.95,0.3,0), area 37.4mm2, adj f0,f1,f4,f267
  f270: cylinder r=69.85mm len=4.99mm, axis (0,0,1), area 28.1mm2, adj f0,f1,f271,f272
  f271: plane 7.14x5.36mm, normal (0.54,0.84,0), area 37.4mm2, adj f0,f1,f4,f270
  f272: plane 7.14x5.04mm, normal (-0.61,-0.79,0), area 37.4mm2, adj f0,f1,f4,f270
  f273: cylinder r=69.85mm len=6.07mm, axis (0,0,1), area 28.1mm2, adj f0,f1,f274,f275
  f274: plane 7.14x6.3mm, normal (0.99,0.13,0), area 37.4mm2, adj f0,f1,f4,f273
  f275: plane 7.14x6.34mm, normal (-1,-0.04,0), area 37.4mm2, adj f0,f1,f4,f273
PLACE A rot(axis=(0,0,1),180deg) t=(-60.66,92.13,5.74)mm
PLACE B t=(-60.66,92.13,81.94)mm
MATE fastened A.f1 <-> B.f4  axis (0,0,1) through (-60.66,92.13,81.94)mm
